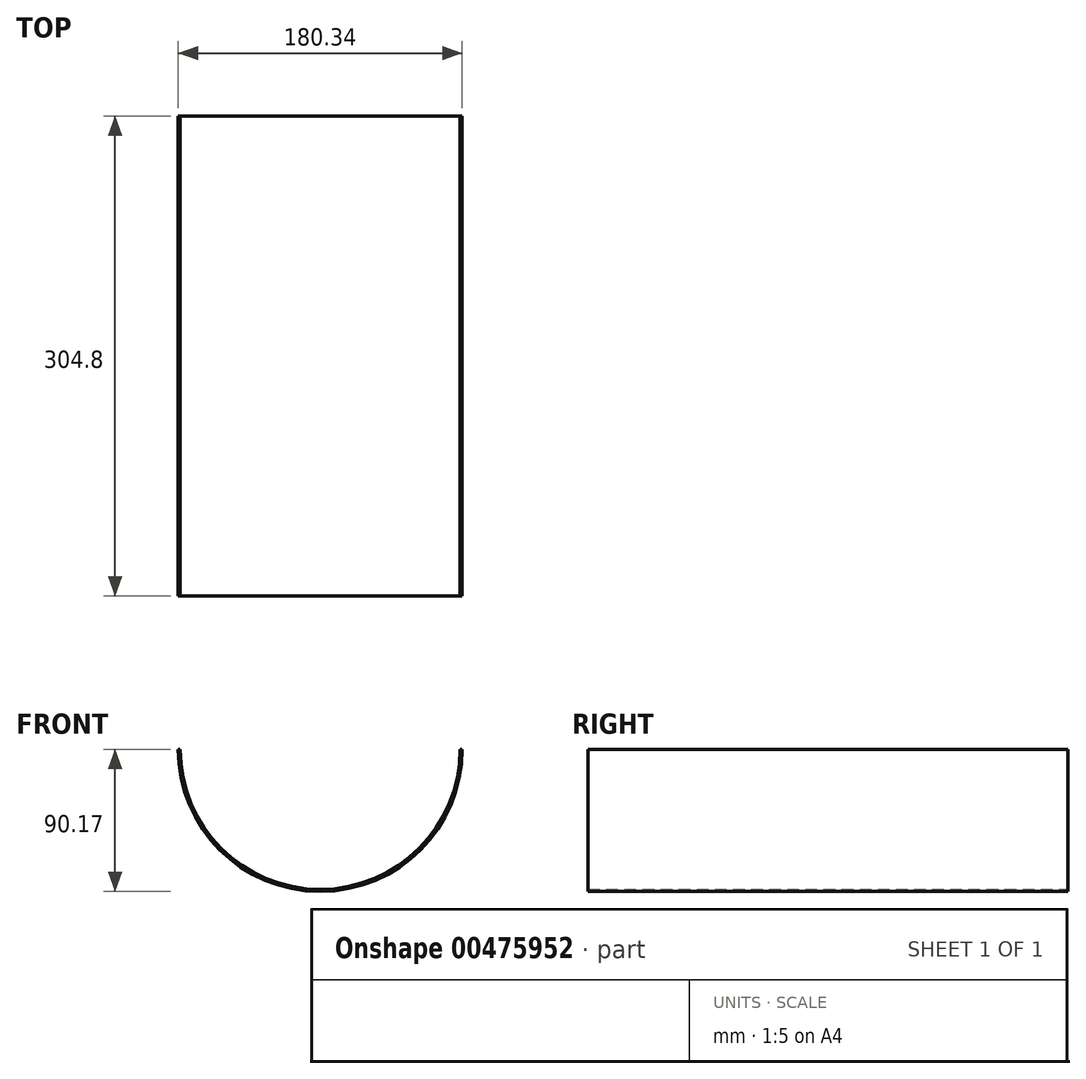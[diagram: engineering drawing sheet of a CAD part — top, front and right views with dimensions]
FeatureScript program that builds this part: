
annotation { "Feature Type Name" : "Feature", "Feature Type Description" : "" }
export const myFeature = defineFeature(function(context is Context, id is Id, definition is map)
    precondition{}
    {
        {
            var Q0;
            Q0=qCreatedBy(makeId("Front.planeOp"),FACE);
            var sketch = newSketch(context, id + "F0", { "sketchPlane" : qUnion([Q0])});
            skArc(sketch, "E0", {"start": v(-90.17, 0) * mm, "mid": v(0, -90.17) * mm, "end": v(90.17, 0) * mm});
            skArc(sketch, "E1", {"start": v(-88.9, 0) * mm, "mid": v(0, -88.9) * mm, "end": v(88.9, 0) * mm});
            skLineSegment(sketch, "E2", {"start": v(-90.17, 0) * mm, "end": v(-88.9, 0) * mm});
            skLineSegment(sketch, "E3", {"start": v(90.17, 0) * mm, "end": v(88.9, 0) * mm});
            skSolve(sketch);
        }
        {
            var Q0;
            Q0 = qSketchRegion(id + "F0", true);
            extrude(context, id + "F1", {"entities" : qUnion([Q0]), "depth" : 152.4 * mm});
        }
        {
            var Q0;
            Q0=makeQuery(id+"F1.opExtrude","CAP_FACE",FACE,{"disambiguationData":[OSD([sQuery(id+"F0.wireOp",EDGE,"E0"),sQuery(id+"F0.wireOp",EDGE,"E1"),sQuery(id+"F0.wireOp",EDGE,"E2"),sQuery(id+"F0.wireOp",EDGE,"E3")])],"isStart":true});
            extrude(context, id + "F2", {"entities" : qUnion([Q0]), "operationType" : NewBodyOperationType.ADD, "depth" : 152.4 * mm});
        }
    });
